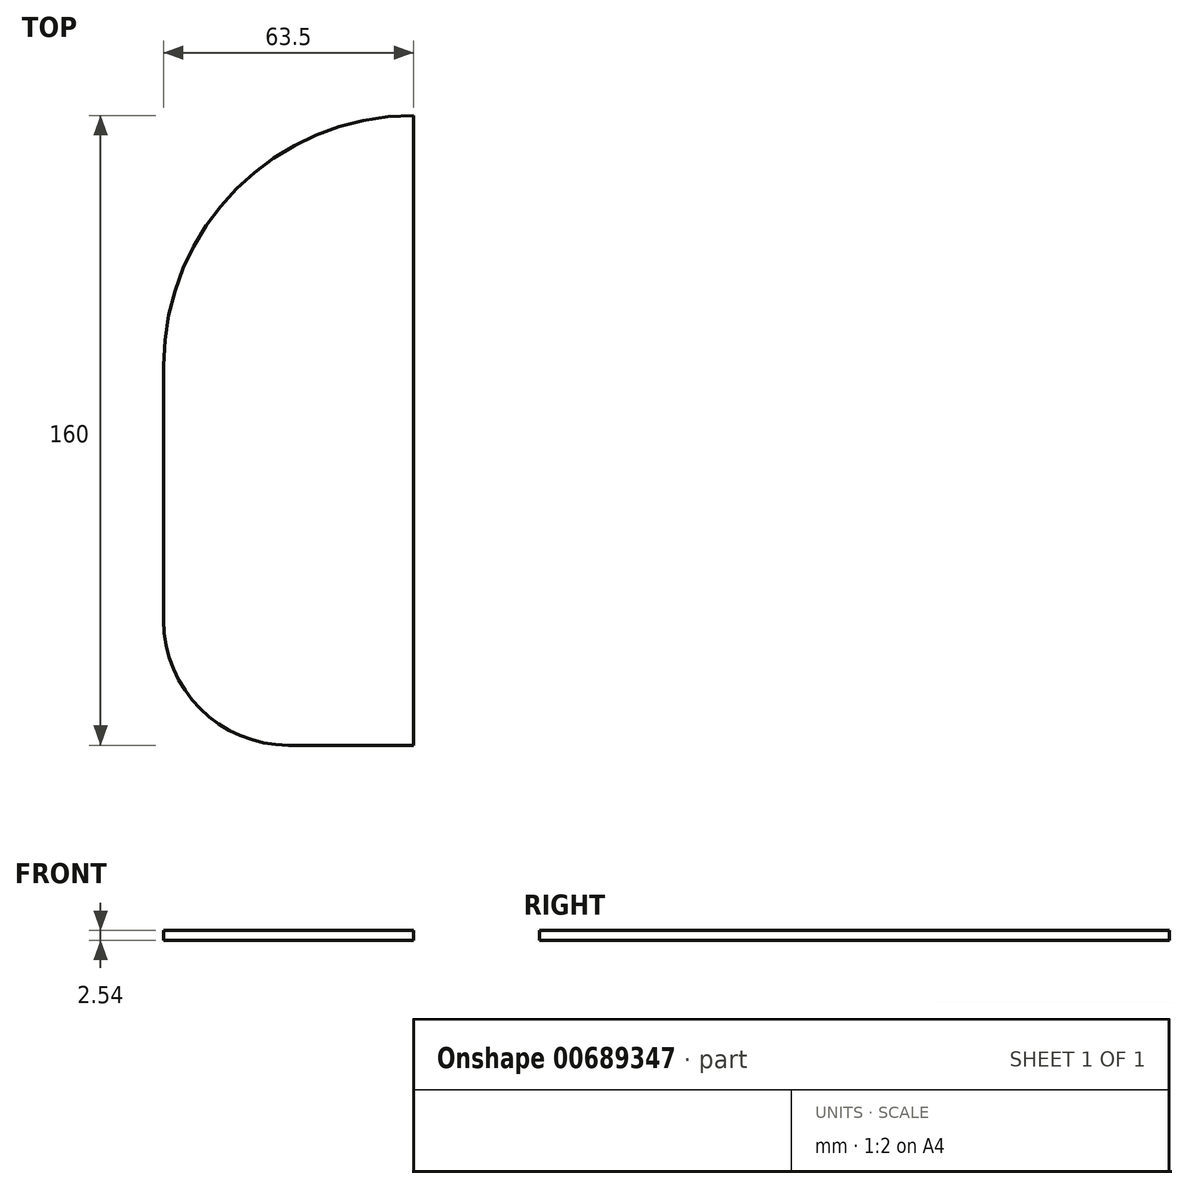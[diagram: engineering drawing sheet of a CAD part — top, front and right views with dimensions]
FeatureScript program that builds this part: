
annotation { "Feature Type Name" : "Feature", "Feature Type Description" : "" }
export const myFeature = defineFeature(function(context is Context, id is Id, definition is map)
    precondition{}
    {
        {
            var Q0;
            Q0=qCreatedBy(makeId("Top.planeOp"),FACE);
            var sketch = newSketch(context, id + "F0", { "sketchPlane" : qUnion([Q0])});
            skLineSegment(sketch, "E0.bottom", {"start": v(14.4, 121.56) * mm, "end": v(14.4, 121.56) * mm});
            skLineSegment(sketch, "E0.top", {"start": v(-17.34, -38.44) * mm, "end": v(14.4, -38.44) * mm});
            skLineSegment(sketch, "E0.left", {"start": v(-49.1, 58.06) * mm, "end": v(-49.1, -6.69) * mm});
            skLineSegment(sketch, "E0.right", {"start": v(14.4, 121.56) * mm, "end": v(14.4, -38.44) * mm});
            skPoint(sketch, "E1.visualSharp", {"position": v(-49.1, 121.56) * mm});
            skArc(sketch, "E1.filletArc", {"start": v(14.4, 121.56) * mm, "mid": v(-30.5, 102.97) * mm, "end": v(-49.1, 58.06) * mm});
            skPoint(sketch, "E2.visualSharp", {"position": v(-49.1, -38.44) * mm});
            skArc(sketch, "E2.filletArc", {"start": v(-49.1, -6.69) * mm, "mid": v(-39.8, -29.14) * mm, "end": v(-17.34, -38.44) * mm});
            skSolve(sketch);
        }
        {
            var Q0;
            Q0=makeQuery(id+"F0.imprint","IMPRINT",FACE,{"disambiguationData":[TD([[makeQuery(id+"F0.imprint","IMPRINT",EDGE,{"derivedFrom":sQuery(id+"F0.wireOp",EDGE,"E0.top")}),1.0]])]});
            extrude(context, id + "F1", {"entities" : qUnion([Q0]), "depth" : 2.54 * mm, "offsetDistance" : 25.4 * mm});
        }
    });
